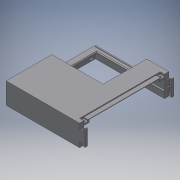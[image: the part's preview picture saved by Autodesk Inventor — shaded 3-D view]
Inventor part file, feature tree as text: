
AUTODESK INVENTOR PART (.ipt)
format: ipt  version: 2016 SP2 (Build 200236200, 236)  size: 885,760 bytes
history: native  units: mm
features: sketch x24, other x5, thread x2, revolve x2
ambient origin geometry x8: Origin, YZ Plane, XZ Plane, XY Plane, X Axis, Y Axis, Z Axis, Center Point
bodies: Volumenkörper2 (feature_tree), Volumenkörper3 (feature_tree), Volumenkörper1 (feature_tree)
feature tree (33):
  other  "Case_side_back.ipt"
  thread  "Gewinde1"  [1 undecoded]
  thread  "Gewinde2"  [1 undecoded]
  revolve  "Umdrehung1"
  other  "Spirale1"
  revolve  "Umdrehung2"
  other  "Spirale2"
  other  "Volumenkörper1::Case_side_back.ipt"
  other  "Bezeichnung1"
  sketch  "Skizze1"  dims[d3=10.0mm d4=0.0mm]
  sketch  "Skizze2"  dims[d5=60.0deg d6=0.240125mm d7=0.240125mm]
  sketch  "Skizze3"  dims[d10=1.5mm]
  sketch  "Skizze4"  dims[d12=60.0deg]
  sketch  "Skizze7"  dims[d14=0.0mm]
  sketch  "Skizze8"  dims[d15=1.5015mm d16=7.0mm d17=10.0mm d18=0.0mm d19=0.0mm d20=0.0mm d21=0.0mm d22=0.0mm]
  sketch  "Skizze9"  dims[d23=60.0deg d24=0.240125mm d25=0.240125mm]
  sketch  "Skizze10"  dims[d28=1.5mm]
  sketch  "Skizze11"  dims[d30=60.0deg]
  sketch  "Skizze12"  dims[d32=0.0mm]
  sketch  "Skizze13"  dims[d33=1.5015mm d34=7.0mm d35=10.0mm d36=0.0mm d37=0.0mm d38=0.0mm d39=0.0mm d40=0.0mm]
  sketch  "Skizze14"
  sketch  "Skizze15"
  sketch  "Skizze16"
  sketch  "Skizze17"
  sketch  "Skizze18"
  sketch  "Skizze19"
  sketch  "Skizze20"
  sketch  "Skizze21"
  sketch  "Skizze22"
  sketch  "Skizze23"
  sketch  "Skizze24"
  sketch  "Skizze25"
  sketch  "Skizze26"
note: 2 required parameter values undecoded (feature->parameter linkage not recoverable at this tier; creation-order binding heuristic only, values carry confidence <= 0.55)
